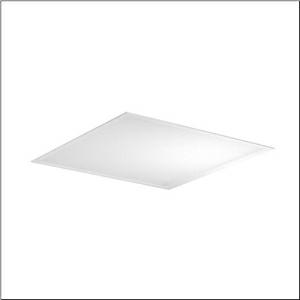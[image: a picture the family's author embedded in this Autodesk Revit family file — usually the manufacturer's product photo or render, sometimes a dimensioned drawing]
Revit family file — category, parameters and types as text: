
# Revit family: apollon_21_square_51mq12wd2414
name_source: partatom
category: Lighting Fixtures
units: mm (PartAtom-declared; Revit-internal decimal feet)

## family parameters
Cut with Voids When Loaded = No
Host = Face
Light Source = No
Part Type = Normal
Room Calculation Point = No
Round Connector Dimension = Use Diameter
Shared = No

## types (1)
- Apollon 21 square (1 x LED, 4200 lm, 24.7 W, 4000K)
    Apparent Load = 25 VA
    CIE Flux Codes = 60 87 97 100 100
    Color Rendering = 80
    Color Temperature = 4000K
    Default Elevation = 1800 mm
    Description = Apollon 21 square, office luminaire, primary optical cover: micro prismatic cover, of PMMA, CAT 2 (L<= 3000cd/m²), light emission: direct distribution, primary light characteristic: symmetric, installation type: lay-in mounting, LED, rated luminous flux: 4.200lm, luminous efficacy: 170lm/W, light colour: 840, colour temperature: 4000K, control gear: DALI 2, Multilumen, with terminal, 5-pole, mains connection: 220..240V, AC/DC, 0/50..60Hz, rated input power: 24.7W, housing, of aluminium, coated, traffic white (RAL 9016), module: M600, length: 595mm, width: 595mm, height: 55mm, recess depth: 180mm, housing upper side, of sheet steel, galvanised, protection rating (complete): IP20, protection rating (lamp compartment, on room side): IP50, insulation class (complete): insulation class II (safety insulation), certification: CE, ENEC, impact resistance: IK03, permissible operating ambient temperature: -20..+45°C, permissible storage temperature: -40..+80°C, standard: EN 60598-2-22, packaging unit: 1 piece
    Height = 0 mm  [stored 0 ft]
    Lamp = 1 x LED
    Lamp Light Flux = 4200 lm
    Lamp Power = 24.7 W
    Lamp count = 1
    Length = 595 mm
    Luminous efficacy = 170 lm/W
    Manufacturer = Siteco
    ModVariant = No
    Model = 51MQ12WD2414
    Mounting Place = Ceiling
    Mounting Type = Recessed
    Number of Poles = 1
    OnlyDefault = Yes
    Power Factor = 1
    Product Name = Apollon 21 square
    Product group = office luminaire | ceiling recessed
    ProductGroupID = 401
    Protection Class = Protection class II
    Protection Degree = IP 20
    RLX_Detail_Level = 1
    RLX_Emergency_Light_Flux = 0 lm
    RLX_Emergency_Type = 0
    RLX_Emergency_Type_DB = No
    RlxData = <blob elided: 12561 chars, md5=262f1a06>
    Socket = socket
    Standby Power = 0 W
    System Light Flux = 4200 lm
    System Power = 25 W
    Type Comments = Product without accessories
    Type Image = l_1291049.jpg
    URL = http://relux.com
    VarID = ---
    Voltage = 0 V
    Weight = 0.00 kg
    Width = 595 mm

note: [stored X ft] marks values corroborated as IEEE doubles in the binary element streams (Revit-internal decimal feet)

## geometry (parser evidence)
native form markers: Sweep x10
no freeform markers — native parametric forms only
